# Revit family: Safety & Protection_Barrier_UltiGroup_Highway Rail
name_source: partatom
category: Generic Models
revit_build: Autodesk Revit Architecture 2016 (Build: 20150220_1215(x64)
units: mm (PartAtom-declared; Revit-internal decimal feet)

## family parameters
Always vertical = Yes
Can host rebar = No
Cut with Voids When Loaded = No
OmniClass Number = 23.30.80.17.11
OmniClass Title = Impact Guard Rails
Part Type = Normal
Room Calculation Point = No
Round Connector Dimension = Use Diameter
Shared = No
Work Plane-Based = No

## types (4) — shared parameters
Base Plate thickness = 20 mm  [stored 0.0656168 ft]
Bolts = Bolts
Description = Gauge 12 (2.7mm) Highway Flex Rail
Fax = 07 846 2467
Galvanised Steel = Galvanised Steel
Manufacturer = UltiGroup
Model = Ulti Highway Rail
Rail height = 470 mm  [stored 1.54199 ft]
Send Message = http://ultigroup.co.nz
URL = www.ultigroup.co.nz
zero-valued in all types: InstallationGroup_ANZRS, ModifiedIssue_ANZRS

## per-type parameters (varying)
| type | Guard Rail | Mid Post | Post 1 | Post 1 Bolt | Post 2 | Post 2 Bolt | Rail length |
| Type 1 | Yes | Yes | Yes | Yes | Yes | Yes | 3810 mm  [stored 12.5 ft] |
| Type 2 | Yes | Yes | No | No | Yes | Yes | 4130 mm  [stored 13.5499 ft] |
| Type 3 | Yes | Yes | Yes | No | Yes | Yes | 4130 mm  [stored 13.5499 ft] |
| Type 4 | No | No | Yes | No | No | No | 4130 mm  [stored 13.5499 ft] |

note: [stored X ft] marks values corroborated as IEEE doubles in the binary element streams (Revit-internal decimal feet)

## geometry (parser evidence)
native form markers: Blend x4, Sweep x8
no freeform markers — native parametric forms only
